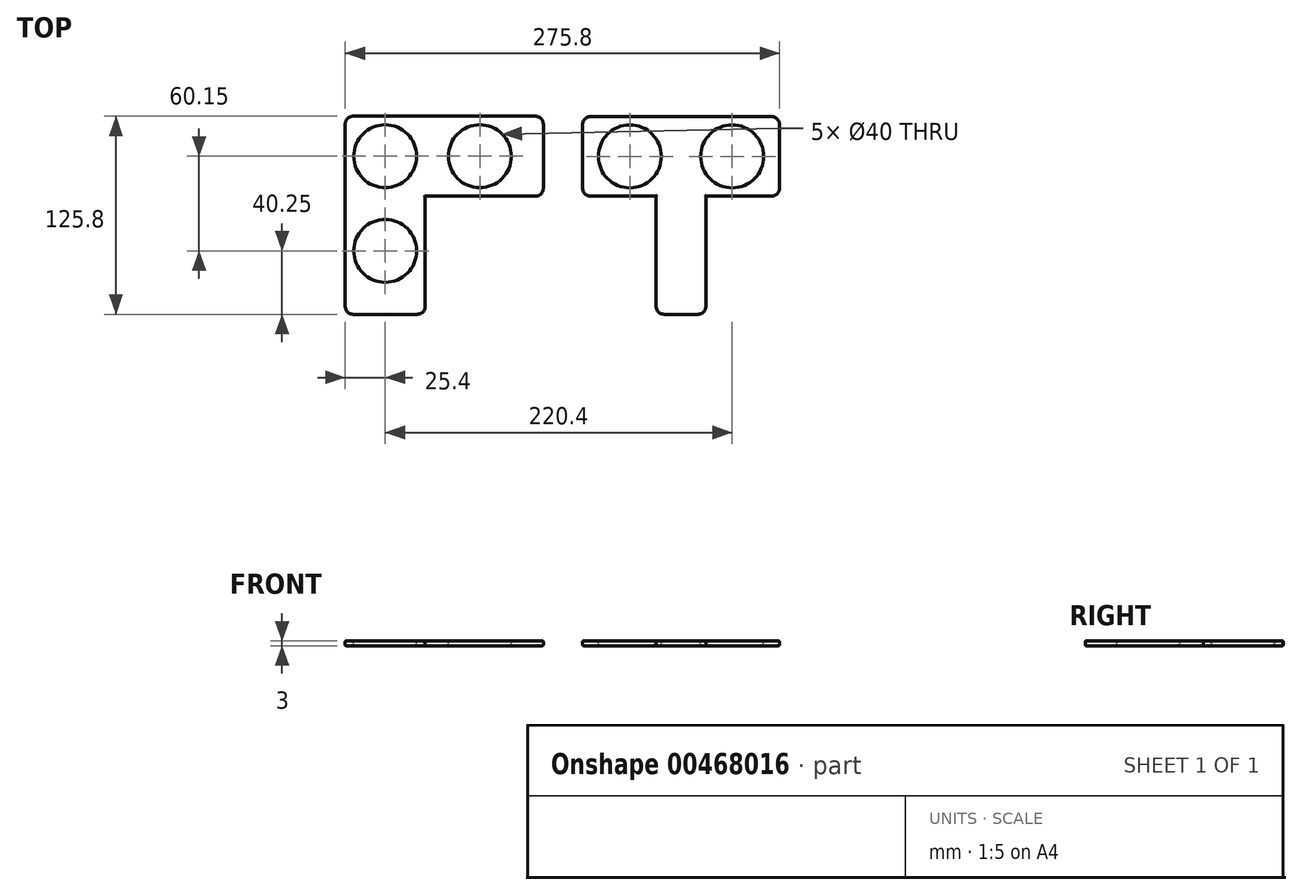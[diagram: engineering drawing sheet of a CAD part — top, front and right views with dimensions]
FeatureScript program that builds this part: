
annotation { "Feature Type Name" : "Feature", "Feature Type Description" : "" }
export const myFeature = defineFeature(function(context is Context, id is Id, definition is map)
    precondition{}
    {
        {
            var Q0;
            Q0=qCreatedBy(makeId("Top.planeOp"),FACE);
            var sketch = newSketch(context, id + "F0", { "sketchPlane" : qUnion([Q0])});
            skLineSegment(sketch, "E0.bottom", {"start": v(0, 0) * mm, "end": v(75, 0) * mm});
            skLineSegment(sketch, "E0.top", {"start": v(0, 50.8) * mm, "end": v(75, 50.8) * mm});
            skLineSegment(sketch, "E0.left", {"start": v(0, 0) * mm, "end": v(0, 50.8) * mm});
            skLineSegment(sketch, "E0.right", {"start": v(75, 0) * mm, "end": v(75, 50.8) * mm});
            skLineSegment(sketch, "E1.bottom", {"start": v(0, 50.8) * mm, "end": v(-50.8, 50.8) * mm});
            skLineSegment(sketch, "E1.top", {"start": v(0, -75) * mm, "end": v(-50.8, -75) * mm});
            skLineSegment(sketch, "E1.left", {"start": v(0, 50.8) * mm, "end": v(0, -75) * mm});
            skLineSegment(sketch, "E1.right", {"start": v(-50.8, 50.8) * mm, "end": v(-50.8, -75) * mm});
            skSolve(sketch);
        }
        {
            var Q0;
            Q0=makeQuery(id+"F0.imprint","IMPRINT",FACE,{"disambiguationData":[TD([[makeQuery(id+"F0.imprint","IMPRINT",EDGE,{"derivedFrom":sQuery(id+"F0.wireOp",EDGE,"E0.left")}),1.0]])]});
            var Q1;
            Q1=makeQuery(id+"F0.imprint","IMPRINT",FACE,{"disambiguationData":[TD([[makeQuery(id+"F0.imprint","IMPRINT",EDGE,{"derivedFrom":sQuery(id+"F0.wireOp",EDGE,"E0.bottom")}),1.0]])]});
            extrude(context, id + "F1", {"entities" : qUnion([Q0, Q1]), "depth" : 3 * mm, "offsetDistance" : 25 * mm});
        }
        {
            var Q0;
            Q0=makeQuery(id+"F1.opExtrude","SWEPT_EDGE",EDGE,{"disambiguationData":[OSD([sQuery(id+"F0.wireOp",EDGE,"E1.top"),sQuery(id+"F0.wireOp",EDGE,"E1.left")])]});
            var Q1;
            Q1=makeQuery(id+"F1.opExtrude","SWEPT_EDGE",EDGE,{"disambiguationData":[OSD([sQuery(id+"F0.wireOp",EDGE,"E1.top"),sQuery(id+"F0.wireOp",EDGE,"E1.right")])]});
            var Q2;
            Q2=makeQuery(id+"F1.opExtrude","SWEPT_EDGE",EDGE,{"disambiguationData":[OSD([sQuery(id+"F0.wireOp",EDGE,"E0.bottom"),sQuery(id+"F0.wireOp",EDGE,"E0.right")])]});
            var Q3;
            Q3=makeQuery(id+"F1.opExtrude","SWEPT_EDGE",EDGE,{"disambiguationData":[OSD([sQuery(id+"F0.wireOp",EDGE,"E0.top"),sQuery(id+"F0.wireOp",EDGE,"E0.right")])]});
            var Q4;
            Q4=makeQuery(id+"F1.opExtrude","SWEPT_EDGE",EDGE,{"disambiguationData":[OSD([sQuery(id+"F0.wireOp",EDGE,"E1.bottom"),sQuery(id+"F0.wireOp",EDGE,"E1.right")])]});
            fillet(context, id + "F2", {"entities" : qUnion([Q0, Q1, Q2, Q3, Q4]), "radius" : 5 * mm, "tangentPropagation" : true, "allowEdgeOverflow" : false});
        }
        {
            var Q0;
            Q0=makeQuery(id+"F1.opExtrude","CAP_EDGE",EDGE,{"disambiguationData":[OSD([sQuery(id+"F0.wireOp",EDGE,"E0.bottom")])],"isStart":false});
            var Q1;
            Q1=makeQuery(id+"F1.opExtrude","CAP_EDGE",EDGE,{"disambiguationData":[OSD([sQuery(id+"F0.wireOp",EDGE,"E0.bottom")])],"isStart":true});
            fillet(context, id + "F3", {"entities" : qUnion([Q0, Q1]), "radius" : 0.5 * mm, "tangentPropagation" : true, "allowEdgeOverflow" : false});
        }
        {
            var Q0;
            Q0=makeQuery(id+"F1.opExtrude","CAP_FACE",FACE,{"disambiguationData":[OSD([sQuery(id+"F0.wireOp",EDGE,"E0.bottom"),sQuery(id+"F0.wireOp",EDGE,"E0.top"),sQuery(id+"F0.wireOp",EDGE,"E0.right"),sQuery(id+"F0.wireOp",EDGE,"E1.bottom"),sQuery(id+"F0.wireOp",EDGE,"E1.top"),sQuery(id+"F0.wireOp",EDGE,"E1.left"),sQuery(id+"F0.wireOp",EDGE,"E1.right")])],"isStart":false});
            var sketch = newSketch(context, id + "F4", { "sketchPlane" : qUnion([Q0])});
            skCircle(sketch, "E2", {"center": v(-25.4, -34.75) * mm, "radius": 20 * mm});
            skPoint(sketch, "E2.centerSnap0", {"position": v(-0.5, -34.75) * mm});
            skPoint(sketch, "E2.centerSnap1", {"position": v(-25.4, -74.5) * mm});
            skCircle(sketch, "E3", {"center": v(34.75, 25.4) * mm, "radius": 20 * mm});
            skPoint(sketch, "E3.centerSnap0", {"position": v(34.75, 0.5) * mm});
            skPoint(sketch, "E3.centerSnap1", {"position": v(74.5, 25.4) * mm});
            skCircle(sketch, "E4", {"center": v(-25.4, 25.4) * mm, "radius": 20 * mm});
            skSolve(sketch);
        }
        {
            var Q0;
            Q0=makeQuery(id+"F4.imprint","IMPRINT",FACE,{"disambiguationData":[TD([[makeQuery(id+"F4.imprint","IMPRINT",EDGE,{"derivedFrom":sQuery(id+"F4.wireOp",EDGE,"E4")}),1.0]])]});
            var Q1;
            Q1=makeQuery(id+"F4.imprint","IMPRINT",FACE,{"disambiguationData":[TD([[makeQuery(id+"F4.imprint","IMPRINT",EDGE,{"derivedFrom":sQuery(id+"F4.wireOp",EDGE,"E2")}),1.0]])]});
            var Q2;
            Q2=makeQuery(id+"F4.imprint","IMPRINT",FACE,{"disambiguationData":[TD([[makeQuery(id+"F4.imprint","IMPRINT",EDGE,{"derivedFrom":sQuery(id+"F4.wireOp",EDGE,"E3")}),1.0]])]});
            extrude(context, id + "F5", {"entities" : qUnion([Q0, Q1, Q2]), "operationType" : NewBodyOperationType.REMOVE, "oppositeDirection" : true, "depth" : 25 * mm, "offsetDistance" : 25 * mm});
        }
        {
            var Q0;
            Q0=qCreatedBy(makeId("Top.planeOp"),FACE);
            var sketch = newSketch(context, id + "F6", { "sketchPlane" : qUnion([Q0])});
            skLineSegment(sketch, "E5.bottom", {"start": v(100, 0) * mm, "end": v(225, 0) * mm});
            skLineSegment(sketch, "E5.top", {"start": v(100, 50.6) * mm, "end": v(225, 50.6) * mm});
            skLineSegment(sketch, "E5.left", {"start": v(100, 0) * mm, "end": v(100, 50.6) * mm});
            skLineSegment(sketch, "E5.right", {"start": v(225, 0) * mm, "end": v(225, 50.6) * mm});
            skLineSegment(sketch, "E6.bottom", {"start": v(178.28, 0) * mm, "end": v(146.73, 0) * mm});
            skLineSegment(sketch, "E6.top", {"start": v(178.27, -75) * mm, "end": v(146.72, -75) * mm});
            skLineSegment(sketch, "E6.left", {"start": v(178.27, 0) * mm, "end": v(178.27, -75) * mm});
            skLineSegment(sketch, "E6.right", {"start": v(146.72, 0) * mm, "end": v(146.72, -75) * mm});
            skPoint(sketch, "E6.middle", {"position": v(162.5, -37.5) * mm});
            skPoint(sketch, "E6.middle.positionSnap0", {"position": v(162.5, 0) * mm});
            skPoint(sketch, "E6.centerSnap0", {"position": v(162.5, 0) * mm});
            skSolve(sketch);
        }
        {
            var Q0;
            Q0=makeQuery(id+"F6.imprint","IMPRINT",FACE,{"disambiguationData":[TD([[makeQuery(id+"F6.imprint","IMPRINT",EDGE,{"derivedFrom":sQuery(id+"F6.wireOp",EDGE,"E5.top")}),-1.0]])]});
            var Q1;
            Q1=makeQuery(id+"F6.imprint","IMPRINT",FACE,{"disambiguationData":[TD([[makeQuery(id+"F6.imprint","IMPRINT",EDGE,{"derivedFrom":sQuery(id+"F6.wireOp",EDGE,"E6.top")}),-1.0]])]});
            extrude(context, id + "F7", {"entities" : qUnion([Q0, Q1]), "depth" : 3 * mm, "offsetDistance" : 25 * mm});
        }
        {
            var Q0;
            Q0=makeQuery(id+"F7.opExtrude","CAP_FACE",FACE,{"disambiguationData":[OSD([sQuery(id+"F6.wireOp",EDGE,"E5.bottom"),sQuery(id+"F6.wireOp",EDGE,"E5.top"),sQuery(id+"F6.wireOp",EDGE,"E5.left"),sQuery(id+"F6.wireOp",EDGE,"E5.right"),sQuery(id+"F6.wireOp",EDGE,"E6.top"),sQuery(id+"F6.wireOp",EDGE,"E6.left"),sQuery(id+"F6.wireOp",EDGE,"E6.right")])],"isStart":false});
            var sketch = newSketch(context, id + "F8", { "sketchPlane" : qUnion([Q0])});
            skCircle(sketch, "E7", {"center": v(130, 25.3) * mm, "radius": 20 * mm});
            skPoint(sketch, "E7.centerSnap0", {"position": v(100, 25.3) * mm});
            skCircle(sketch, "E8", {"center": v(195, 25.3) * mm, "radius": 20 * mm});
            skPoint(sketch, "E8.centerSnap0", {"position": v(225, 25.3) * mm});
            skSolve(sketch);
        }
        {
            var Q0;
            Q0=makeQuery(id+"F8.imprint","IMPRINT",FACE,{"disambiguationData":[TD([[makeQuery(id+"F8.imprint","IMPRINT",EDGE,{"derivedFrom":sQuery(id+"F8.wireOp",EDGE,"E8")}),1.0]])]});
            var Q1;
            Q1=makeQuery(id+"F8.imprint","IMPRINT",FACE,{"disambiguationData":[TD([[makeQuery(id+"F8.imprint","IMPRINT",EDGE,{"derivedFrom":sQuery(id+"F8.wireOp",EDGE,"E7")}),1.0]])]});
            extrude(context, id + "F9", {"entities" : qUnion([Q0, Q1]), "operationType" : NewBodyOperationType.REMOVE, "oppositeDirection" : true, "depth" : 25 * mm, "offsetDistance" : 25 * mm});
        }
        {
            var Q0;
            Q0=makeQuery(id+"F7.opExtrude","SWEPT_EDGE",EDGE,{"disambiguationData":[OSD([sQuery(id+"F6.wireOp",EDGE,"E6.top"),sQuery(id+"F6.wireOp",EDGE,"E6.right")])]});
            var Q1;
            Q1=makeQuery(id+"F7.opExtrude","SWEPT_EDGE",EDGE,{"disambiguationData":[OSD([sQuery(id+"F6.wireOp",EDGE,"E6.top"),sQuery(id+"F6.wireOp",EDGE,"E6.left")])]});
            var Q2;
            Q2=makeQuery(id+"F7.opExtrude","SWEPT_EDGE",EDGE,{"disambiguationData":[OSD([sQuery(id+"F6.wireOp",EDGE,"E5.bottom"),sQuery(id+"F6.wireOp",EDGE,"E5.right")])]});
            var Q3;
            Q3=makeQuery(id+"F7.opExtrude","SWEPT_EDGE",EDGE,{"disambiguationData":[OSD([sQuery(id+"F6.wireOp",EDGE,"E5.bottom"),sQuery(id+"F6.wireOp",EDGE,"E5.left")])]});
            var Q4;
            Q4=makeQuery(id+"F7.opExtrude","SWEPT_EDGE",EDGE,{"disambiguationData":[OSD([sQuery(id+"F6.wireOp",EDGE,"E5.top"),sQuery(id+"F6.wireOp",EDGE,"E5.left")])]});
            var Q5;
            Q5=makeQuery(id+"F7.opExtrude","SWEPT_EDGE",EDGE,{"disambiguationData":[OSD([sQuery(id+"F6.wireOp",EDGE,"E5.top"),sQuery(id+"F6.wireOp",EDGE,"E5.right")])]});
            fillet(context, id + "F10", {"entities" : qUnion([Q0, Q1, Q2, Q3, Q4, Q5]), "radius" : 5 * mm, "tangentPropagation" : true, "allowEdgeOverflow" : false});
        }
        {
            var Q0;
            Q0=makeQuery(id+"F7.opExtrude","CAP_EDGE",EDGE,{"disambiguationData":[OSD([sQuery(id+"F6.wireOp",EDGE,"E5.left")])],"isStart":false});
            var Q1;
            Q1=makeQuery(id+"F7.opExtrude","CAP_EDGE",EDGE,{"disambiguationData":[OSD([sQuery(id+"F6.wireOp",EDGE,"E5.left")])],"isStart":true});
            var Q2;
            Q2=makeQuery(id+"F7.opExtrude","CAP_EDGE",EDGE,{"disambiguationData":[OSD([sQuery(id+"F6.wireOp",EDGE,"E6.right")])],"isStart":true});
            var Q3;
            Q3=makeQuery(id+"F7.opExtrude","CAP_EDGE",EDGE,{"disambiguationData":[OSD([sQuery(id+"F6.wireOp",EDGE,"E6.right")])],"isStart":false});
            fillet(context, id + "F11", {"entities" : qUnion([Q0, Q1, Q2, Q3]), "radius" : 0.5 * mm, "tangentPropagation" : true, "allowEdgeOverflow" : false});
        }
    });
